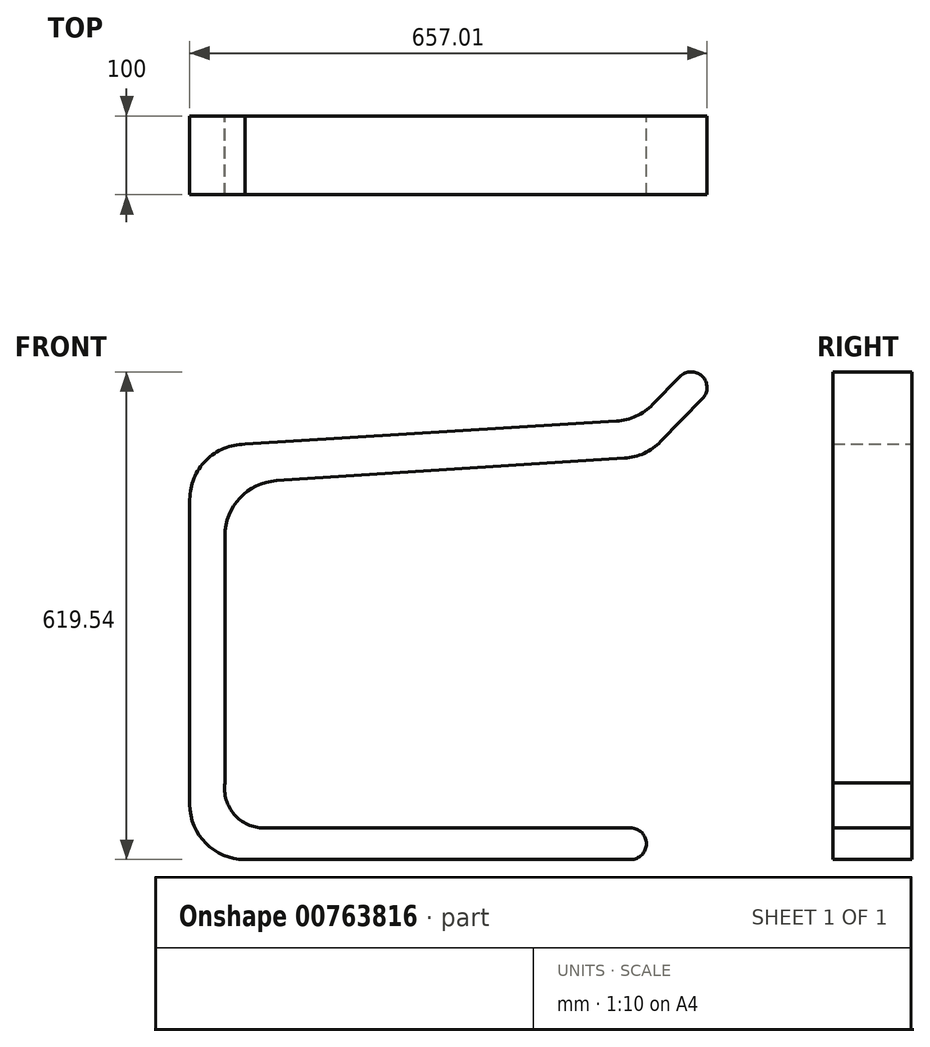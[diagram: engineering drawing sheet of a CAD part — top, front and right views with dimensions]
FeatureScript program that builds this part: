
annotation { "Feature Type Name" : "Feature", "Feature Type Description" : "" }
export const myFeature = defineFeature(function(context is Context, id is Id, definition is map)
    precondition{}
    {
        {
            var Q0;
            Q0=qCreatedBy(makeId("Front.planeOp"),FACE);
            var sketch = newSketch(context, id + "F0", { "sketchPlane" : qUnion([Q0])});
            skLineSegment(sketch, "E0", {"start": v(558.95, 17.86) * mm, "end": v(68.95, 17.86) * mm});
            skLineSegment(sketch, "E1", {"start": v(-1.05, 87.86) * mm, "end": v(-1.05, 475.4) * mm});
            skPoint(sketch, "E2.endSnap0", {"position": v(9, 470) * mm});
            skPoint(sketch, "E3.visualSharp", {"position": v(-1.05, 511.61) * mm});
            skArc(sketch, "E3.filletArc", {"start": v(68.99, 545.4) * mm, "mid": v(19.47, 524.91) * mm, "end": v(-1.05, 475.4) * mm});
            skLineSegment(sketch, "E4", {"start": v(68.99, 545.4) * mm, "end": v(541.1, 574.74) * mm});
            skLineSegment(sketch, "E5", {"start": v(586.87, 595.73) * mm, "end": v(621.62, 631.36) * mm});
            skPoint(sketch, "E6.visualSharp", {"position": v(-1.05, 17.86) * mm});
            skArc(sketch, "E6.filletArc", {"start": v(-1.05, 87.86) * mm, "mid": v(19.45, 38.36) * mm, "end": v(68.95, 17.86) * mm});
            skLineSegment(sketch, "E7", {"start": v(578.95, 37.86) * mm, "end": v(578.95, 37.86) * mm});
            skLineSegment(sketch, "E8", {"start": v(558.95, 57.86) * mm, "end": v(93.23, 57.86) * mm});
            skPoint(sketch, "E9.visualSharp", {"position": v(39.39, 57.86) * mm});
            skArc(sketch, "E9.filletArc", {"start": v(43.75, 115) * mm, "mid": v(55.44, 75.13) * mm, "end": v(93.23, 57.86) * mm});
            skLineSegment(sketch, "E10", {"start": v(43.75, 115) * mm, "end": v(43.75, 401.56) * mm});
            skLineSegment(sketch, "E11", {"start": v(43.75, 401.56) * mm, "end": v(43.75, 429.26) * mm});
            skLineSegment(sketch, "E12", {"start": v(109.24, 499.12) * mm, "end": v(551.38, 527.65) * mm});
            skPoint(sketch, "E13.visualSharp", {"position": v(43.75, 494.9) * mm});
            skArc(sketch, "E13.filletArc", {"start": v(109.24, 499.12) * mm, "mid": v(62.68, 477.14) * mm, "end": v(43.75, 429.26) * mm});
            skLineSegment(sketch, "E14", {"start": v(597.05, 548.7) * mm, "end": v(650.3, 603.44) * mm});
            skLineSegment(sketch, "E15", {"start": v(649.92, 631.7) * mm, "end": v(649.9, 631.72) * mm});
            skPoint(sketch, "E16.orphan", {"position": v(636.6, 646.73) * mm});
            skPoint(sketch, "E17.orphan", {"position": v(634.52, 646.73) * mm});
            skPoint(sketch, "E18.visualSharp", {"position": v(568.03, 576.41) * mm});
            skArc(sketch, "E18.filletArc", {"start": v(541.1, 574.74) * mm, "mid": v(565.93, 580.97) * mm, "end": v(586.87, 595.73) * mm});
            skPoint(sketch, "E19.visualSharp", {"position": v(578.26, 529.39) * mm});
            skArc(sketch, "E19.filletArc", {"start": v(551.38, 527.65) * mm, "mid": v(576.17, 533.93) * mm, "end": v(597.05, 548.7) * mm});
            skPoint(sketch, "E20.visualSharp", {"position": v(635.58, 645.68) * mm});
            skArc(sketch, "E20.filletArc", {"start": v(649.9, 631.72) * mm, "mid": v(635.69, 637.4) * mm, "end": v(621.62, 631.36) * mm});
            skPoint(sketch, "E21.visualSharp", {"position": v(664.22, 617.75) * mm});
            skArc(sketch, "E21.filletArc", {"start": v(650.3, 603.44) * mm, "mid": v(655.96, 617.65) * mm, "end": v(649.92, 631.7) * mm});
            skPoint(sketch, "E22.visualSharp", {"position": v(578.95, 57.86) * mm});
            skArc(sketch, "E22.filletArc", {"start": v(578.95, 37.86) * mm, "mid": v(573.1, 52) * mm, "end": v(558.95, 57.86) * mm});
            skPoint(sketch, "E23.visualSharp", {"position": v(578.95, 17.86) * mm});
            skArc(sketch, "E23.filletArc", {"start": v(558.95, 17.86) * mm, "mid": v(573.1, 23.72) * mm, "end": v(578.95, 37.86) * mm});
            skLineSegment(sketch, "E24", {"start": v(-1.05, 421.1) * mm, "end": v(43.75, 421.1) * mm});
            skLineSegment(sketch, "E25", {"start": v(-1.05, 127.02) * mm, "end": v(43.75, 127.02) * mm});
            skSolve(sketch);
        }
        {
            var Q0;
            {var subQ0=sQuery(id+"F0.wireOp",EDGE,"E24");Q0=makeQuery(id+"F0.imprint","IMPRINT",FACE,{"disambiguationData":[TD([[makeQuery(id+"F0.imprint","IMPRINT",EDGE,{"derivedFrom":subQ0}),-1.0]])]});}
            var Q1;
            Q1=makeQuery(id+"F0.imprint","IMPRINT",FACE,{"disambiguationData":[TD([[makeQuery(id+"F0.imprint","IMPRINT",EDGE,{"derivedFrom":sQuery(id+"F0.wireOp",EDGE,"E0")}),-1.0]])]});
            extrude(context, id + "F1", {"entities" : qUnion([Q0, Q1]), "depth" : 100 * mm, "offsetDistance" : 25 * mm});
        }
        {
            var Q0;
            {var subQ3=sQuery(id+"F0.wireOp",EDGE,"E3.filletArc");Q0=makeQuery(id+"F0.imprint","IMPRINT",FACE,{"disambiguationData":[TD([[makeQuery(id+"F0.imprint","IMPRINT",EDGE,{"derivedFrom":subQ3}),1.0]])]});}
            extrude(context, id + "F2", {"entities" : qUnion([Q0]), "operationType" : NewBodyOperationType.ADD, "depth" : 100 * mm, "offsetDistance" : 25 * mm});
        }
    });
